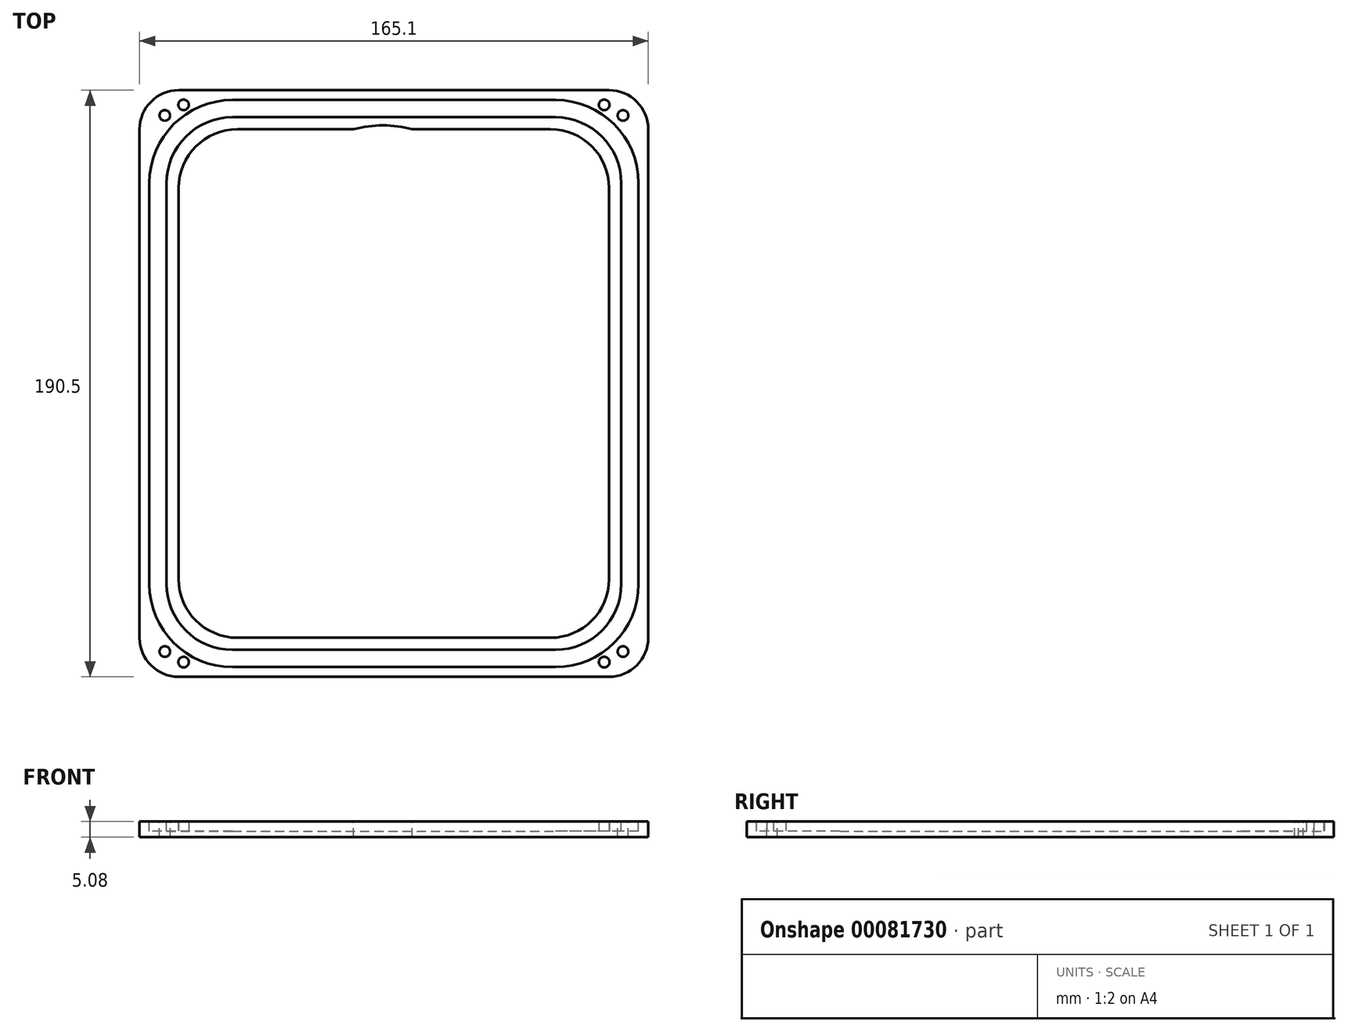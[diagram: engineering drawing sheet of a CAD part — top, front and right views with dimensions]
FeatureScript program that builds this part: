
annotation { "Feature Type Name" : "Feature", "Feature Type Description" : "" }
export const myFeature = defineFeature(function(context is Context, id is Id, definition is map)
    precondition{}
    {
        {
            var Q0;
            Q0=qCreatedBy(makeId("Top.planeOp"),FACE);
            var sketch = newSketch(context, id + "F0", { "sketchPlane" : qUnion([Q0])});
            skLineSegment(sketch, "E0.bottom", {"start": v(12.7, 0) * mm, "end": v(152.4, 0) * mm});
            skLineSegment(sketch, "E0.top", {"start": v(12.7, 190.5) * mm, "end": v(152.4, 190.5) * mm});
            skLineSegment(sketch, "E0.left", {"start": v(0, 12.7) * mm, "end": v(0, 177.8) * mm});
            skLineSegment(sketch, "E0.right", {"start": v(165.1, 12.7) * mm, "end": v(165.1, 177.8) * mm});
            skPoint(sketch, "E1.visualSharp", {"position": v(0, 190.5) * mm});
            skArc(sketch, "E1.filletArc", {"start": v(12.7, 190.5) * mm, "mid": v(3.72, 186.78) * mm, "end": v(0, 177.8) * mm});
            skPoint(sketch, "E2.visualSharp", {"position": v(165.1, 190.5) * mm});
            skArc(sketch, "E2.filletArc", {"start": v(165.1, 177.8) * mm, "mid": v(161.38, 186.78) * mm, "end": v(152.4, 190.5) * mm});
            skPoint(sketch, "E3.visualSharp", {"position": v(165.1, 0) * mm});
            skArc(sketch, "E3.filletArc", {"start": v(152.4, 0) * mm, "mid": v(161.38, 3.72) * mm, "end": v(165.1, 12.7) * mm});
            skPoint(sketch, "E4.visualSharp", {"position": v(0, 0) * mm});
            skArc(sketch, "E4.filletArc", {"start": v(0, 12.7) * mm, "mid": v(3.72, 3.72) * mm, "end": v(12.7, 0) * mm});
            skLineSegment(sketch, "E5.4", {"start": v(12.7, 177.8) * mm, "end": v(12.7, 177.8) * mm});
            skLineSegment(sketch, "E6.bottom", {"start": v(31.75, 177.8) * mm, "end": v(133.35, 177.8) * mm});
            skLineSegment(sketch, "E6.top", {"start": v(31.75, 12.7) * mm, "end": v(133.35, 12.7) * mm});
            skLineSegment(sketch, "E6.left", {"start": v(12.7, 158.75) * mm, "end": v(12.7, 31.75) * mm});
            skLineSegment(sketch, "E6.right", {"start": v(152.4, 158.75) * mm, "end": v(152.4, 31.75) * mm});
            skArc(sketch, "E7.filletArc", {"start": v(31.75, 177.8) * mm, "mid": v(18.28, 172.22) * mm, "end": v(12.7, 158.75) * mm});
            skArc(sketch, "E8.filletArc", {"start": v(152.4, 158.75) * mm, "mid": v(146.82, 172.22) * mm, "end": v(133.35, 177.8) * mm});
            skArc(sketch, "E9.filletArc", {"start": v(133.35, 12.7) * mm, "mid": v(146.82, 18.28) * mm, "end": v(152.4, 31.75) * mm});
            skArc(sketch, "E10.filletArc", {"start": v(12.7, 31.75) * mm, "mid": v(18.28, 18.28) * mm, "end": v(31.75, 12.7) * mm});
            skSolve(sketch);
        }
        {
            var Q0;
            Q0 = qSketchRegion(id + "F0", true);
            extrude(context, id + "F1", {"entities" : qUnion([Q0]), "depth" : 5.08 * mm});
        }
        {
            var Q0;
            Q0=makeQuery(id+"F1.opExtrude","CAP_FACE",FACE,{"disambiguationData":[OSD([sQuery(id+"F0.wireOp",EDGE,"E0.bottom"),sQuery(id+"F0.wireOp",EDGE,"E0.top"),sQuery(id+"F0.wireOp",EDGE,"E0.left"),sQuery(id+"F0.wireOp",EDGE,"E0.right"),sQuery(id+"F0.wireOp",EDGE,"E1.filletArc"),sQuery(id+"F0.wireOp",EDGE,"E2.filletArc"),sQuery(id+"F0.wireOp",EDGE,"E3.filletArc"),sQuery(id+"F0.wireOp",EDGE,"E4.filletArc"),sQuery(id+"F0.wireOp",EDGE,"E5.0"),sQuery(id+"F0.wireOp",EDGE,"E5.1"),sQuery(id+"F0.wireOp",EDGE,"E5.2"),sQuery(id+"F0.wireOp",EDGE,"E5.3"),sQuery(id+"F0.wireOp",EDGE,"E5.4"),sQuery(id+"F0.wireOp",EDGE,"E5.5"),sQuery(id+"F0.wireOp",EDGE,"E5.6"),sQuery(id+"F0.wireOp",EDGE,"E5.7")])],"isStart":false});
            var sketch = newSketch(context, id + "F2", { "sketchPlane" : qUnion([Q0])});
            skPoint(sketch, "E11.firstSnap0", {"position": v(3.72, 186.78) * mm});
            skLineSegment(sketch, "E12.bottom", {"start": v(30.15, 3.18) * mm, "end": v(134.95, 3.18) * mm});
            skLineSegment(sketch, "E12.top", {"start": v(30.15, 187.33) * mm, "end": v(134.95, 187.33) * mm});
            skLineSegment(sketch, "E12.left", {"start": v(3.18, 30.15) * mm, "end": v(3.17, 160.35) * mm});
            skLineSegment(sketch, "E12.right", {"start": v(161.92, 30.15) * mm, "end": v(161.92, 160.35) * mm});
            skPoint(sketch, "E13.visualSharp", {"position": v(3.17, 187.33) * mm});
            skArc(sketch, "E13.filletArc", {"start": v(30.15, 187.33) * mm, "mid": v(11.08, 179.42) * mm, "end": v(3.17, 160.35) * mm});
            skPoint(sketch, "E14.visualSharp", {"position": v(161.92, 187.33) * mm});
            skArc(sketch, "E14.filletArc", {"start": v(161.92, 160.35) * mm, "mid": v(154.02, 179.42) * mm, "end": v(134.95, 187.33) * mm});
            skPoint(sketch, "E15.visualSharp", {"position": v(161.92, 3.18) * mm});
            skArc(sketch, "E15.filletArc", {"start": v(134.95, 3.18) * mm, "mid": v(154.02, 11.08) * mm, "end": v(161.93, 30.15) * mm});
            skPoint(sketch, "E16.visualSharp", {"position": v(3.18, 3.17) * mm});
            skArc(sketch, "E16.filletArc", {"start": v(3.18, 30.15) * mm, "mid": v(11.08, 11.08) * mm, "end": v(30.15, 3.18) * mm});
            skArc(sketch, "E17.0", {"start": v(8.76, 30.15) * mm, "mid": v(15.03, 15.03) * mm, "end": v(30.15, 8.76) * mm});
            skLineSegment(sketch, "E17.1", {"start": v(30.15, 8.76) * mm, "end": v(134.95, 8.76) * mm});
            skLineSegment(sketch, "E17.2", {"start": v(8.76, 30.15) * mm, "end": v(8.76, 160.35) * mm});
            skArc(sketch, "E17.3", {"start": v(134.95, 8.76) * mm, "mid": v(150.07, 15.03) * mm, "end": v(156.34, 30.15) * mm});
            skArc(sketch, "E17.4", {"start": v(30.15, 181.74) * mm, "mid": v(15.03, 175.47) * mm, "end": v(8.76, 160.35) * mm});
            skLineSegment(sketch, "E17.5", {"start": v(30.15, 181.74) * mm, "end": v(134.95, 181.74) * mm});
            skArc(sketch, "E17.6", {"start": v(156.34, 160.35) * mm, "mid": v(150.07, 175.47) * mm, "end": v(134.95, 181.74) * mm});
            skLineSegment(sketch, "E17.7", {"start": v(156.34, 30.15) * mm, "end": v(156.34, 160.35) * mm});
            skSolve(sketch);
        }
        {
            var Q0;
            Q0 = qSketchRegion(id + "F2", true);
            extrude(context, id + "F3", {"entities" : qUnion([Q0]), "operationType" : NewBodyOperationType.REMOVE, "oppositeDirection" : true, "depth" : 3.17 * mm});
        }
        {
            var Q0;
            Q0=makeQuery(id+"F1.opExtrude","CAP_FACE",FACE,{"disambiguationData":[OSD([sQuery(id+"F0.wireOp",EDGE,"E0.bottom"),sQuery(id+"F0.wireOp",EDGE,"E0.top"),sQuery(id+"F0.wireOp",EDGE,"E0.left"),sQuery(id+"F0.wireOp",EDGE,"E0.right"),sQuery(id+"F0.wireOp",EDGE,"E1.filletArc"),sQuery(id+"F0.wireOp",EDGE,"E2.filletArc"),sQuery(id+"F0.wireOp",EDGE,"E3.filletArc"),sQuery(id+"F0.wireOp",EDGE,"E4.filletArc"),sQuery(id+"F0.wireOp",EDGE,"E6.bottom"),sQuery(id+"F0.wireOp",EDGE,"E6.top"),sQuery(id+"F0.wireOp",EDGE,"E6.left"),sQuery(id+"F0.wireOp",EDGE,"E6.right"),sQuery(id+"F0.wireOp",EDGE,"E7.filletArc"),sQuery(id+"F0.wireOp",EDGE,"E8.filletArc"),sQuery(id+"F0.wireOp",EDGE,"E9.filletArc"),sQuery(id+"F0.wireOp",EDGE,"E10.filletArc")])],"isStart":true});
            var sketch = newSketch(context, id + "F4", { "sketchPlane" : qUnion([Q0])});
            skLineSegment(sketch, "E18", {"start": v(0, -142.21) * mm, "end": v(0, -190.5) * mm, "construction": true});
            skLineSegment(sketch, "E19", {"start": v(0, -190.5) * mm, "end": v(29.51, -160.99) * mm, "construction": true});
            skLineSegment(sketch, "E20", {"start": v(165.1, -140.35) * mm, "end": v(165.1, -190.5) * mm, "construction": true});
            skLineSegment(sketch, "E21", {"start": v(165.1, -190.5) * mm, "end": v(133.35, -158.75) * mm, "construction": true});
            skLineSegment(sketch, "E22", {"start": v(165.1, -41.87) * mm, "end": v(165.1, 0) * mm, "construction": true});
            skLineSegment(sketch, "E23", {"start": v(165.1, 0) * mm, "end": v(133.83, -31.27) * mm, "construction": true});
            skLineSegment(sketch, "E24", {"start": v(0, -42.8) * mm, "end": v(0, 0) * mm, "construction": true});
            skLineSegment(sketch, "E25", {"start": v(0, 0) * mm, "end": v(32.9, -32.9) * mm, "construction": true});
            skPoint(sketch, "E26", {"position": v(8.2, -182.3) * mm});
            skPoint(sketch, "E27", {"position": v(156.9, -182.3) * mm});
            skPoint(sketch, "E28", {"position": v(156.9, -8.2) * mm});
            skPoint(sketch, "E29", {"position": v(8.2, -8.2) * mm});
            skSolve(sketch);
        }
        {
            var Q0;
            Q0=sQuery(id+"F4.wireOp",VERTEX,"E26");
            var Q1;
            Q1=sQuery(id+"F4.wireOp",VERTEX,"E27");
            var Q2;
            Q2=sQuery(id+"F4.wireOp",VERTEX,"E28");
            var Q3;
            Q3=sQuery(id+"F4.wireOp",VERTEX,"E29");
            var Q4;
            Q4=makeQuery(id+"F1.opExtrude","SWEPT_BODY",BODY,{"disambiguationData":[OSD([sQuery(id+"F0.wireOp",EDGE,"E0.bottom"),sQuery(id+"F0.wireOp",EDGE,"E0.top"),sQuery(id+"F0.wireOp",EDGE,"E0.left"),sQuery(id+"F0.wireOp",EDGE,"E0.right"),sQuery(id+"F0.wireOp",EDGE,"E1.filletArc"),sQuery(id+"F0.wireOp",EDGE,"E2.filletArc"),sQuery(id+"F0.wireOp",EDGE,"E3.filletArc"),sQuery(id+"F0.wireOp",EDGE,"E4.filletArc"),sQuery(id+"F0.wireOp",EDGE,"E6.bottom"),sQuery(id+"F0.wireOp",EDGE,"E6.top"),sQuery(id+"F0.wireOp",EDGE,"E6.left"),sQuery(id+"F0.wireOp",EDGE,"E6.right"),sQuery(id+"F0.wireOp",EDGE,"E7.filletArc"),sQuery(id+"F0.wireOp",EDGE,"E8.filletArc"),sQuery(id+"F0.wireOp",EDGE,"E9.filletArc"),sQuery(id+"F0.wireOp",EDGE,"E10.filletArc")])]});
            hole(context, id + "F5", {"style" : HoleStyle.SIMPLE, "endStyle" : HoleEndStyle.THROUGH, "standardTappedOrClearance" : lookupTablePath({ "standard" : "ANSI", "engagement" : "75%", "pitch" : "32 tpi", "size" : "#8", "type" : "Tapped" }), "standardBlindInLast" : lookupTablePath({ "standard" : "ANSI", "engagement" : "75%", "pitch" : "32 tpi", "size" : "#8", "type" : "Tapped" }), "holeDiameter" : 3.45 * mm, "locations" : qUnion([Q0, Q1, Q2, Q3]), "scope" : qUnion([Q4]), "isTappedThrough" : true, "majorDiameter" : 4.17 * mm, "showTappedDepth" : true, "startStyle" : HoleStartStyle.PART});
        }
        {
            var Q0;
            {var subQ0=sQuery(id+"F0.wireOp",EDGE,"E4.filletArc");var subQ1=sQuery(id+"F0.wireOp",EDGE,"E3.filletArc");var subQ2=sQuery(id+"F0.wireOp",EDGE,"E2.filletArc");var subQ3=sQuery(id+"F0.wireOp",EDGE,"E1.filletArc");var subQ4=sQuery(id+"F0.wireOp",EDGE,"E0.bottom");var subQ5=sQuery(id+"F0.wireOp",EDGE,"E0.top");var subQ6=sQuery(id+"F0.wireOp",EDGE,"E0.left");var subQ7=sQuery(id+"F0.wireOp",EDGE,"E0.right");Q0=makeQuery(id+"F3.boolean.opBoolean","SPLIT",FACE,{"disambiguationData":[TD([makeQuery(id+"F1.opExtrude","SWEPT_FACE",FACE,{"disambiguationData":[OSD([subQ4])]})])],"derivedFrom":makeQuery(id+"F1.opExtrude","CAP_FACE",FACE,{"disambiguationData":[OSD([subQ4,subQ5,subQ6,subQ7,subQ3,subQ2,subQ1,subQ0,sQuery(id+"F0.wireOp",EDGE,"E6.bottom"),sQuery(id+"F0.wireOp",EDGE,"E6.top"),sQuery(id+"F0.wireOp",EDGE,"E6.left"),sQuery(id+"F0.wireOp",EDGE,"E6.right"),sQuery(id+"F0.wireOp",EDGE,"E7.filletArc"),sQuery(id+"F0.wireOp",EDGE,"E8.filletArc"),sQuery(id+"F0.wireOp",EDGE,"E9.filletArc"),sQuery(id+"F0.wireOp",EDGE,"E10.filletArc")])],"isStart":false})});}
            var sketch = newSketch(context, id + "F6", { "sketchPlane" : qUnion([Q0])});
            skPoint(sketch, "E30", {"position": v(14.3, 4.78) * mm});
            skPoint(sketch, "E31", {"position": v(150.8, 4.78) * mm});
            skPoint(sketch, "E32", {"position": v(14.3, 185.72) * mm});
            skPoint(sketch, "E33", {"position": v(150.8, 185.72) * mm});
            skSolve(sketch);
        }
        {
            var Q0;
            Q0=sQuery(id+"F6.wireOp",VERTEX,"E32");
            var Q1;
            Q1=sQuery(id+"F6.wireOp",VERTEX,"E33");
            var Q2;
            Q2=sQuery(id+"F6.wireOp",VERTEX,"E30");
            var Q3;
            Q3=sQuery(id+"F6.wireOp",VERTEX,"E31");
            var Q4;
            Q4=makeQuery(id+"F1.opExtrude","SWEPT_BODY",BODY,{"disambiguationData":[OSD([sQuery(id+"F0.wireOp",EDGE,"E0.bottom"),sQuery(id+"F0.wireOp",EDGE,"E0.top"),sQuery(id+"F0.wireOp",EDGE,"E0.left"),sQuery(id+"F0.wireOp",EDGE,"E0.right"),sQuery(id+"F0.wireOp",EDGE,"E1.filletArc"),sQuery(id+"F0.wireOp",EDGE,"E2.filletArc"),sQuery(id+"F0.wireOp",EDGE,"E3.filletArc"),sQuery(id+"F0.wireOp",EDGE,"E4.filletArc"),sQuery(id+"F0.wireOp",EDGE,"E6.bottom"),sQuery(id+"F0.wireOp",EDGE,"E6.top"),sQuery(id+"F0.wireOp",EDGE,"E6.left"),sQuery(id+"F0.wireOp",EDGE,"E6.right"),sQuery(id+"F0.wireOp",EDGE,"E7.filletArc"),sQuery(id+"F0.wireOp",EDGE,"E8.filletArc"),sQuery(id+"F0.wireOp",EDGE,"E9.filletArc"),sQuery(id+"F0.wireOp",EDGE,"E10.filletArc")])]});
            hole(context, id + "F7", {"style" : HoleStyle.SIMPLE, "endStyle" : HoleEndStyle.THROUGH, "holeDiameter" : 3.43 * mm, "locations" : qUnion([Q0, Q1, Q2, Q3]), "scope" : qUnion([Q4]), "isTappedThrough" : true, "startStyle" : HoleStartStyle.PART});
        }
        {
            var Q0;
            {var subQ0=sQuery(id+"F0.wireOp",EDGE,"E10.filletArc");var subQ1=sQuery(id+"F0.wireOp",EDGE,"E6.bottom");var subQ2=sQuery(id+"F0.wireOp",EDGE,"E9.filletArc");var subQ3=sQuery(id+"F0.wireOp",EDGE,"E8.filletArc");var subQ4=sQuery(id+"F0.wireOp",EDGE,"E7.filletArc");var subQ5=sQuery(id+"F0.wireOp",EDGE,"E6.top");var subQ6=sQuery(id+"F0.wireOp",EDGE,"E6.left");var subQ7=sQuery(id+"F0.wireOp",EDGE,"E6.right");Q0=makeQuery(id+"F3.boolean.opBoolean","SPLIT",FACE,{"disambiguationData":[TD([makeQuery(id+"F1.opExtrude","SWEPT_FACE",FACE,{"disambiguationData":[OSD([subQ1])]})])],"derivedFrom":makeQuery(id+"F1.opExtrude","CAP_FACE",FACE,{"disambiguationData":[OSD([sQuery(id+"F0.wireOp",EDGE,"E0.bottom"),sQuery(id+"F0.wireOp",EDGE,"E0.top"),sQuery(id+"F0.wireOp",EDGE,"E0.left"),sQuery(id+"F0.wireOp",EDGE,"E0.right"),sQuery(id+"F0.wireOp",EDGE,"E1.filletArc"),sQuery(id+"F0.wireOp",EDGE,"E2.filletArc"),sQuery(id+"F0.wireOp",EDGE,"E3.filletArc"),sQuery(id+"F0.wireOp",EDGE,"E4.filletArc"),subQ1,subQ5,subQ6,subQ7,subQ4,subQ3,subQ2,subQ0])],"isStart":false})});}
            var sketch = newSketch(context, id + "F8", { "sketchPlane" : qUnion([Q0])});
            skCircle(sketch, "E34", {"center": v(79, 142.88) * mm, "radius": 36.2 * mm});
            skSolve(sketch);
        }
        {
            var Q0;
            Q0 = qSketchRegion(id + "F8", true);
            extrude(context, id + "F9", {"entities" : qUnion([Q0]), "operationType" : NewBodyOperationType.REMOVE, "endBound" : BoundingType.THROUGH_ALL, "oppositeDirection" : true, "depth" : 25.4 * mm});
        }
    });
